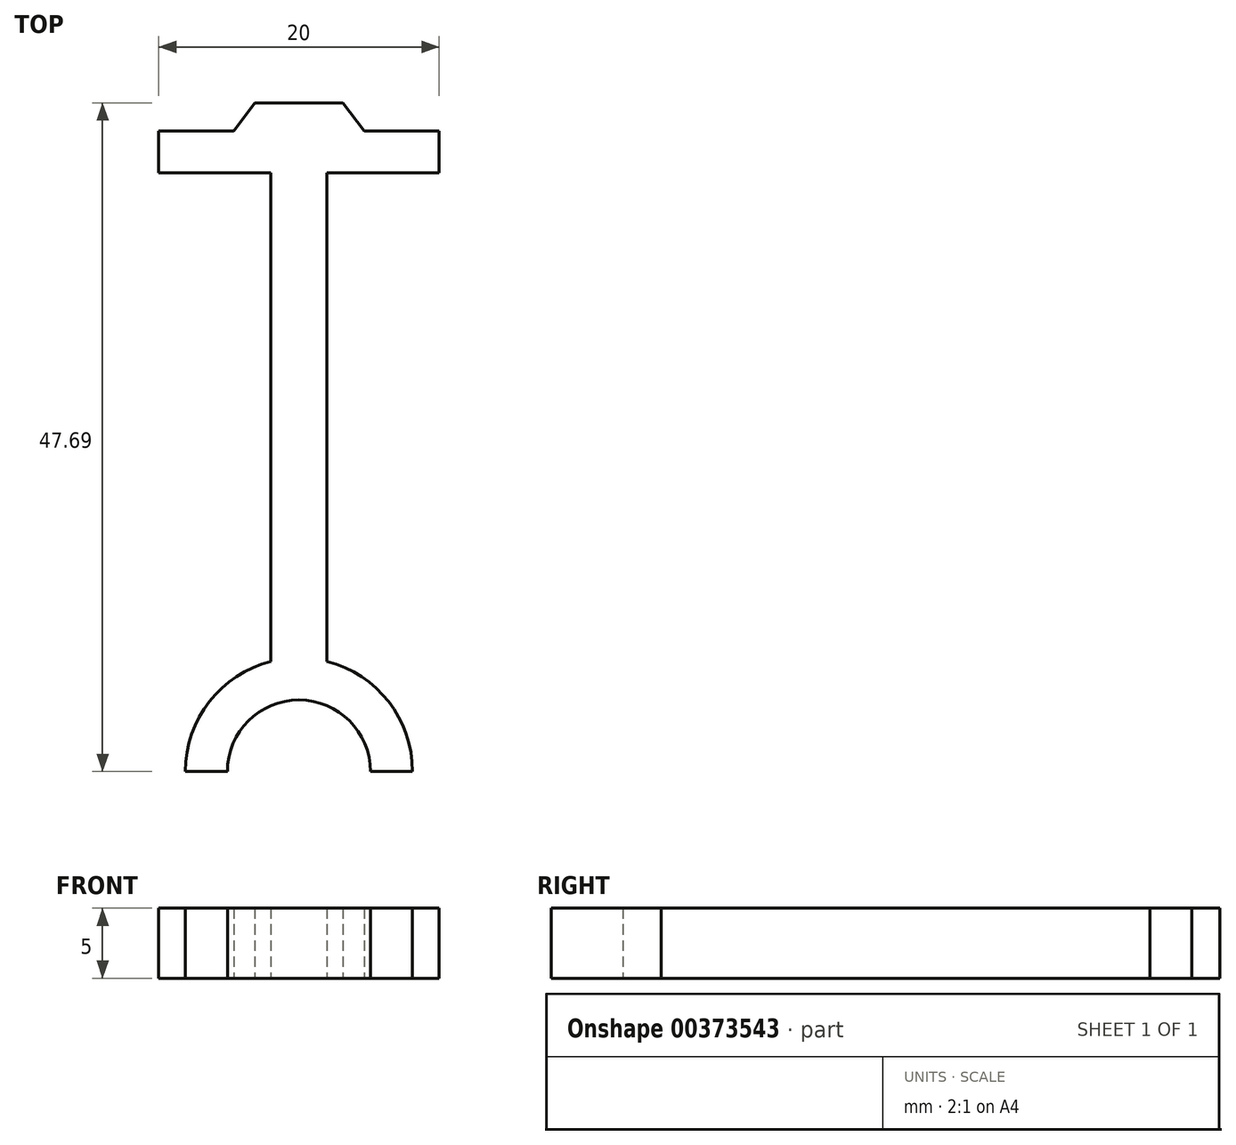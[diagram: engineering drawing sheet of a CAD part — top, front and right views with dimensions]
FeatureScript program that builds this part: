
annotation { "Feature Type Name" : "Feature", "Feature Type Description" : "" }
export const myFeature = defineFeature(function(context is Context, id is Id, definition is map)
    precondition{}
    {
        {
            var Q0;
            Q0=qCreatedBy(makeId("Top.planeOp"),FACE);
            var sketch = newSketch(context, id + "F0", { "sketchPlane" : qUnion([Q0])});
            skArc(sketch, "E0", {"start": v(5.1, 0) * mm, "mid": v(0, 5.1) * mm, "end": v(-5.1, 0) * mm});
            skLineSegment(sketch, "E1", {"start": v(0, 0) * mm, "end": v(0, 44.2) * mm, "construction": true});
            skLineSegment(sketch, "E2.0", {"start": v(2, 4.7) * mm, "end": v(2, 42.7) * mm});
            skLineSegment(sketch, "E3.MirrorCS", {"start": v(-2, 4.7) * mm, "end": v(-2, 42.7) * mm});
            skLineSegment(sketch, "E4.bottom", {"start": v(10, 42.7) * mm, "end": v(-10, 42.7) * mm});
            skLineSegment(sketch, "E4.top", {"start": v(10, 45.7) * mm, "end": v(-10, 45.7) * mm});
            skLineSegment(sketch, "E4.left", {"start": v(10, 42.7) * mm, "end": v(10, 45.7) * mm});
            skLineSegment(sketch, "E4.right", {"start": v(-10, 42.7) * mm, "end": v(-10, 45.7) * mm});
            skPoint(sketch, "E4.middle", {"position": v(0, 44.2) * mm});
            skArc(sketch, "E5.0", {"start": v(8.1, 0) * mm, "mid": v(0, 8.1) * mm, "end": v(-8.1, 0) * mm});
            skLineSegment(sketch, "E6", {"start": v(8.1, 0) * mm, "end": v(5.1, 0) * mm});
            skLineSegment(sketch, "E7.trimOffspring", {"start": v(-5.1, 0) * mm, "end": v(-8.1, 0) * mm});
            skLineSegment(sketch, "E8", {"start": v(-4.65, 45.7) * mm, "end": v(-3.15, 47.7) * mm});
            skLineSegment(sketch, "E9", {"start": v(-3.15, 47.7) * mm, "end": v(3.15, 47.7) * mm});
            skLineSegment(sketch, "E10", {"start": v(3.15, 47.7) * mm, "end": v(4.65, 45.7) * mm});
            skLineSegment(sketch, "E11", {"start": v(0, 44.2) * mm, "end": v(0, 48.83) * mm, "construction": true});
            skLineSegment(sketch, "E12", {"start": v(0, 47.7) * mm, "end": v(0, 48.83) * mm, "construction": true});
            skSolve(sketch);
        }
        {
            var Q0;
            Q0 = qSketchRegion(id + "F0", true);
            extrude(context, id + "F1", {"entities" : qUnion([Q0]), "depth" : 5 * mm});
        }
    });
